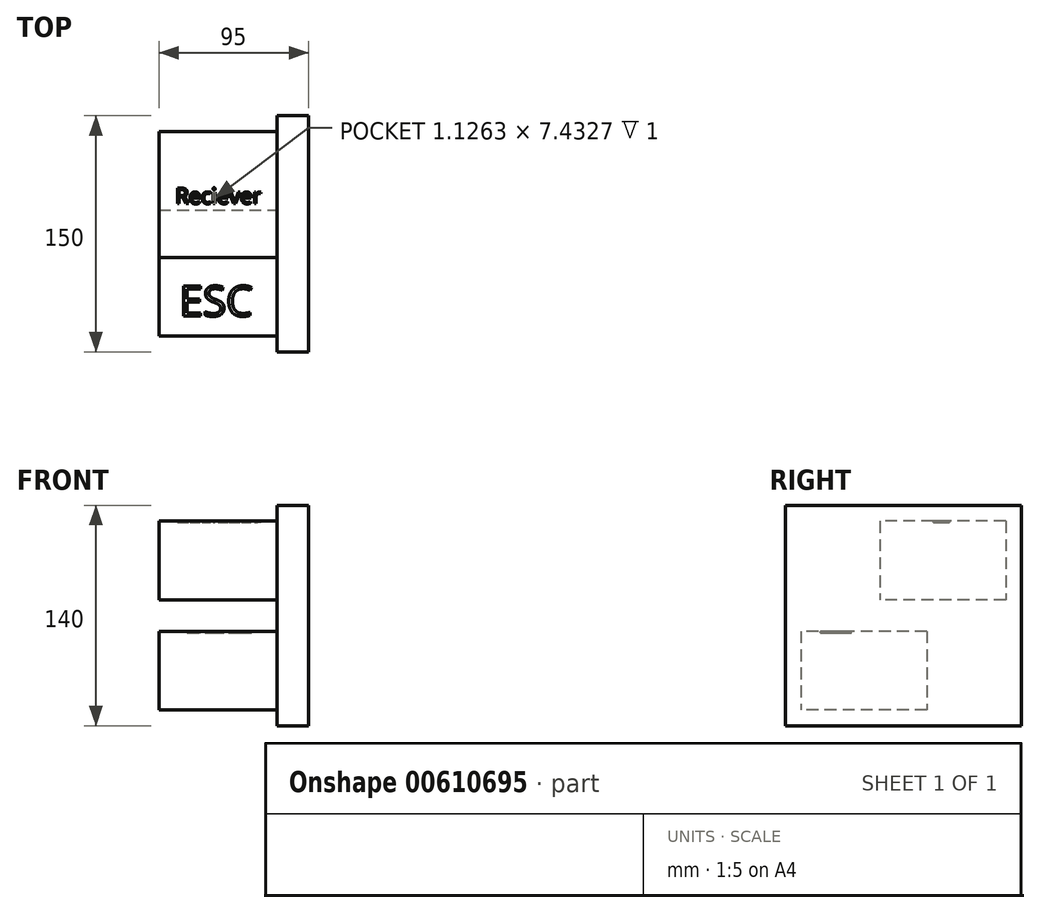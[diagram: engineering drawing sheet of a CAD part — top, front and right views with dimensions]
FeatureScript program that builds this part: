
annotation { "Feature Type Name" : "Feature", "Feature Type Description" : "" }
export const myFeature = defineFeature(function(context is Context, id is Id, definition is map)
    precondition{}
    {
        {
            var Q0;
            Q0=qCreatedBy(makeId("Right.planeOp"),FACE);
            var sketch = newSketch(context, id + "F0", { "sketchPlane" : qUnion([Q0])});
            skLineSegment(sketch, "E0.bottom", {"start": v(0, 0) * mm, "end": v(150, 0) * mm});
            skLineSegment(sketch, "E0.top", {"start": v(0, 140) * mm, "end": v(150, 140) * mm});
            skLineSegment(sketch, "E0.left", {"start": v(0, 0) * mm, "end": v(0, 140) * mm});
            skLineSegment(sketch, "E0.right", {"start": v(150, 0) * mm, "end": v(150, 140) * mm});
            skSolve(sketch);
        }
        {
            var Q0;
            Q0 = qSketchRegion(id + "F0", true);
            extrude(context, id + "F1", {"entities" : qUnion([Q0]), "depth" : 20 * mm, "offsetDistance" : 25 * mm});
        }
        {
            var Q0;
            Q0=makeQuery(id+"F1.opExtrude","CAP_FACE",FACE,{"disambiguationData":[OSD([sQuery(id+"F0.wireOp",EDGE,"E0.bottom"),sQuery(id+"F0.wireOp",EDGE,"E0.top"),sQuery(id+"F0.wireOp",EDGE,"E0.left"),sQuery(id+"F0.wireOp",EDGE,"E0.right")])],"isStart":true});
            var sketch = newSketch(context, id + "F2", { "sketchPlane" : qUnion([Q0])});
            skLineSegment(sketch, "E1.bottom", {"start": v(-140, 130) * mm, "end": v(-60, 130) * mm});
            skLineSegment(sketch, "E1.top", {"start": v(-140, 80) * mm, "end": v(-60, 80) * mm});
            skLineSegment(sketch, "E1.left", {"start": v(-140, 130) * mm, "end": v(-140, 80) * mm});
            skLineSegment(sketch, "E1.right", {"start": v(-60, 130) * mm, "end": v(-60, 80) * mm});
            skLineSegment(sketch, "E2.bottom", {"start": v(-90, 60) * mm, "end": v(-10, 60) * mm});
            skLineSegment(sketch, "E2.top", {"start": v(-90, 10) * mm, "end": v(-10, 10) * mm});
            skLineSegment(sketch, "E2.left", {"start": v(-90, 60) * mm, "end": v(-90, 10) * mm});
            skLineSegment(sketch, "E2.right", {"start": v(-10, 60) * mm, "end": v(-10, 10) * mm});
            skSolve(sketch);
        }
        {
            var Q0;
            Q0=makeQuery(id+"F2.imprint","IMPRINT",FACE,{"disambiguationData":[TD([[makeQuery(id+"F2.imprint","IMPRINT",EDGE,{"derivedFrom":sQuery(id+"F2.wireOp",EDGE,"E1.bottom")}),-1.0]])]});
            var Q1;
            Q1=makeQuery(id+"F2.imprint","IMPRINT",FACE,{"disambiguationData":[TD([[makeQuery(id+"F2.imprint","IMPRINT",EDGE,{"derivedFrom":sQuery(id+"F2.wireOp",EDGE,"E2.bottom")}),-1.0]])]});
            extrude(context, id + "F3", {"entities" : qUnion([Q0, Q1]), "operationType" : NewBodyOperationType.ADD, "depth" : 75 * mm, "offsetDistance" : 25 * mm});
        }
        {
            var Q0;
            Q0=makeQuery(id+"F3.opExtrude","SWEPT_FACE",FACE,{"disambiguationData":[OSD([sQuery(id+"F2.wireOp",EDGE,"E1.bottom")])]});
            var sketch = newSketch(context, id + "F4", { "sketchPlane" : qUnion([Q0])});
            skText(sketch, "E3", { "text": "Reciever", "fontName": "OpenSans-Regular.ttf"});
            const initialGuessF4  = {"E3": [-0.06466, 0.0941, 1, 0, 0.01]};
            skSetInitialGuess(sketch, initialGuessF4);
            skSolve(sketch);
        }
        {
            var Q0;
            Q0=makeQuery(id+"F3.opExtrude","SWEPT_FACE",FACE,{"disambiguationData":[OSD([sQuery(id+"F2.wireOp",EDGE,"E2.bottom")])]});
            var sketch = newSketch(context, id + "F5", { "sketchPlane" : qUnion([Q0])});
            skText(sketch, "E4", { "text": "ESC", "fontName": "OpenSans-Regular.ttf"});
            const initialGuessF5  = {"E4": [-0.06191, 0.02273, 1, 0, 0.01926]};
            skSetInitialGuess(sketch, initialGuessF5);
            skSolve(sketch);
        }
        {
            var Q0;
            Q0 = qSketchRegion(id + "F4", true);
            var Q1;
            Q1 = qSketchRegion(id + "F5", true);
            extrude(context, id + "F6", {"entities" : qUnion([Q0, Q1]), "operationType" : NewBodyOperationType.REMOVE, "oppositeDirection" : true, "depth" : 1 * mm, "offsetDistance" : 25 * mm});
        }
    });
